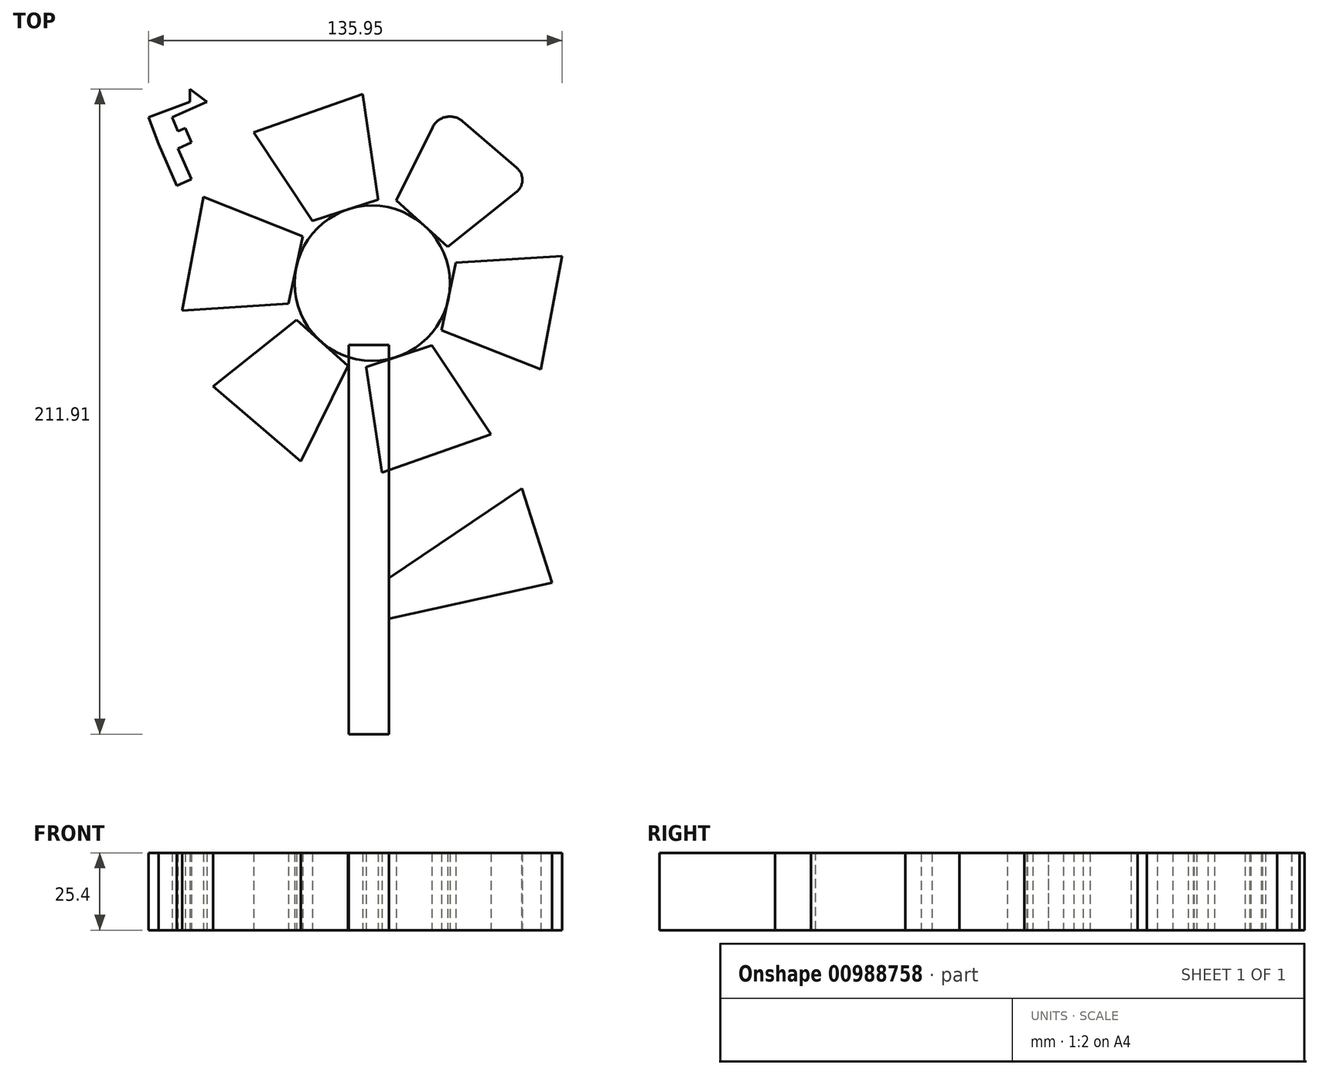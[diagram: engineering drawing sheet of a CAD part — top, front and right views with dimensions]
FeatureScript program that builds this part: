
annotation { "Feature Type Name" : "Feature", "Feature Type Description" : "" }
export const myFeature = defineFeature(function(context is Context, id is Id, definition is map)
    precondition{}
    {
        {
            var Q0;
            Q0=qCreatedBy(makeId("Top.planeOp"),FACE);
            var sketch = newSketch(context, id + "F0", { "sketchPlane" : qUnion([Q0])});
            skCircle(sketch, "E0", {"center": v(0, 0) * mm, "radius": 25.52 * mm});
            skLineSegment(sketch, "E1", {"start": v(7.91, 27.2) * mm, "end": v(24.8, 12.03) * mm});
            skLineSegment(sketch, "E2", {"start": v(24.8, 12.03) * mm, "end": v(52.24, 33.82) * mm});
            skLineSegment(sketch, "E3", {"start": v(52.24, 33.82) * mm, "end": v(29.66, 53.24) * mm});
            skLineSegment(sketch, "E4", {"start": v(19.83, 51.24) * mm, "end": v(7.91, 27.2) * mm});
            skLineSegment(sketch, "E5.1.0", {"start": v(-39, 49.6) * mm, "end": v(-19.6, 20.45) * mm});
            skLineSegment(sketch, "E5.1.1", {"start": v(-3.17, 62.15) * mm, "end": v(-39, 49.6) * mm});
            skLineSegment(sketch, "E5.1.2", {"start": v(1.98, 27.49) * mm, "end": v(-3.17, 62.15) * mm});
            skLineSegment(sketch, "E5.1.3", {"start": v(-19.6, 20.45) * mm, "end": v(1.98, 27.49) * mm});
            skLineSegment(sketch, "E5.2.0", {"start": v(-62.45, -8.97) * mm, "end": v(-27.51, -6.74) * mm});
            skLineSegment(sketch, "E5.2.1", {"start": v(-55.4, 28.33) * mm, "end": v(-62.45, -8.97) * mm});
            skLineSegment(sketch, "E5.2.2", {"start": v(-22.81, 15.46) * mm, "end": v(-55.4, 28.33) * mm});
            skLineSegment(sketch, "E5.2.3", {"start": v(-27.51, -6.74) * mm, "end": v(-22.81, 15.46) * mm});
            skLineSegment(sketch, "E5.3.0", {"start": v(-23.46, -58.57) * mm, "end": v(-7.91, -27.2) * mm});
            skLineSegment(sketch, "E5.3.1", {"start": v(-52.24, -33.82) * mm, "end": v(-23.46, -58.57) * mm});
            skLineSegment(sketch, "E5.3.2", {"start": v(-24.8, -12.03) * mm, "end": v(-52.24, -33.82) * mm});
            skLineSegment(sketch, "E5.3.3", {"start": v(-7.91, -27.2) * mm, "end": v(-24.8, -12.03) * mm});
            skLineSegment(sketch, "E5.4.0", {"start": v(39, -49.6) * mm, "end": v(19.6, -20.45) * mm});
            skLineSegment(sketch, "E5.4.1", {"start": v(3.17, -62.15) * mm, "end": v(39, -49.6) * mm});
            skLineSegment(sketch, "E5.4.2", {"start": v(-1.98, -27.49) * mm, "end": v(3.17, -62.15) * mm});
            skLineSegment(sketch, "E5.4.3", {"start": v(19.6, -20.45) * mm, "end": v(-1.98, -27.49) * mm});
            skLineSegment(sketch, "E5.5.0", {"start": v(62.45, 8.97) * mm, "end": v(27.51, 6.74) * mm});
            skLineSegment(sketch, "E5.5.1", {"start": v(55.4, -28.33) * mm, "end": v(62.45, 8.97) * mm});
            skLineSegment(sketch, "E5.5.2", {"start": v(22.81, -15.46) * mm, "end": v(55.4, -28.33) * mm});
            skLineSegment(sketch, "E5.5.3", {"start": v(27.51, 6.74) * mm, "end": v(22.81, -15.46) * mm});
            skPoint(sketch, "E6.visualSharp", {"position": v(23.46, 58.57) * mm});
            skArc(sketch, "E6.filletArc", {"start": v(29.66, 53.24) * mm, "mid": v(24.25, 54.64) * mm, "end": v(19.83, 51.24) * mm});
            skSolve(sketch);
        }
        {
            var Q0;
            {var subQ0=sQuery(id+"F0.wireOp",EDGE,"E0");var subQ4=makeQuery(id+"F0.imprint","INTERSECT",VERTEX,{"derivedFrom":[subQ0,sQuery(id+"F0.wireOp",EDGE,"E5.1.3")]});Q0=makeQuery(id+"F0.imprint","IMPRINT",FACE,{"disambiguationData":[TD([[makeQuery(id+"F0.imprint","IMPRINT",EDGE,{"disambiguationData":[TD([[subQ4,1.0]])],"derivedFrom":subQ0}),1.0]])]});}
            var Q1;
            {var subQ0=sQuery(id+"F0.wireOp",EDGE,"E2");Q1=makeQuery(id+"F0.imprint","IMPRINT",FACE,{"disambiguationData":[TD([[makeQuery(id+"F0.imprint","IMPRINT",EDGE,{"derivedFrom":subQ0}),1.0]])]});}
            var Q2;
            {var subQ1=sQuery(id+"F0.wireOp",EDGE,"E5.1.0");Q2=makeQuery(id+"F0.imprint","IMPRINT",FACE,{"disambiguationData":[TD([[makeQuery(id+"F0.imprint","IMPRINT",EDGE,{"derivedFrom":subQ1}),1.0]])]});}
            var Q3;
            {var subQ1=sQuery(id+"F0.wireOp",EDGE,"E5.2.0");Q3=makeQuery(id+"F0.imprint","IMPRINT",FACE,{"disambiguationData":[TD([[makeQuery(id+"F0.imprint","IMPRINT",EDGE,{"derivedFrom":subQ1}),1.0]])]});}
            var Q4;
            {var subQ1=sQuery(id+"F0.wireOp",EDGE,"E5.3.0");Q4=makeQuery(id+"F0.imprint","IMPRINT",FACE,{"disambiguationData":[TD([[makeQuery(id+"F0.imprint","IMPRINT",EDGE,{"derivedFrom":subQ1}),1.0]])]});}
            var Q5;
            {var subQ1=sQuery(id+"F0.wireOp",EDGE,"E5.4.0");Q5=makeQuery(id+"F0.imprint","IMPRINT",FACE,{"disambiguationData":[TD([[makeQuery(id+"F0.imprint","IMPRINT",EDGE,{"derivedFrom":subQ1}),1.0]])]});}
            var Q6;
            {var subQ1=sQuery(id+"F0.wireOp",EDGE,"E5.5.0");Q6=makeQuery(id+"F0.imprint","IMPRINT",FACE,{"disambiguationData":[TD([[makeQuery(id+"F0.imprint","IMPRINT",EDGE,{"derivedFrom":subQ1}),1.0]])]});}
            extrude(context, id + "F1", {"entities" : qUnion([Q0, Q1, Q2, Q3, Q4, Q5, Q6]), "depth" : 25.4 * mm, "offsetDistance" : 25.4 * mm});
        }
        {
            var Q0;
            Q0=makeQuery(id+"F1.opExtrude","CAP_FACE",FACE,{"disambiguationData":[OSD([sQuery(id+"F0.wireOp",EDGE,"E5.4.0"),sQuery(id+"F0.wireOp",EDGE,"E5.4.1"),sQuery(id+"F0.wireOp",EDGE,"E5.4.2"),sQuery(id+"F0.wireOp",EDGE,"E5.4.3")])],"isStart":false});
            var sketch = newSketch(context, id + "F2", { "sketchPlane" : qUnion([Q0])});
            skLineSegment(sketch, "E7.bottom", {"start": v(-7.73, -20.32) * mm, "end": v(5.51, -20.32) * mm});
            skLineSegment(sketch, "E7.top", {"start": v(-7.73, -148.1) * mm, "end": v(5.51, -148.1) * mm});
            skLineSegment(sketch, "E7.left", {"start": v(-7.73, -20.32) * mm, "end": v(-7.73, -148.1) * mm});
            skLineSegment(sketch, "E7.right", {"start": v(5.51, -20.32) * mm, "end": v(5.51, -148.1) * mm});
            skSolve(sketch);
        }
        {
            var Q0;
            Q0 = qSketchRegion(id + "F2", true);
            extrude(context, id + "F3", {"entities" : qUnion([Q0]), "oppositeDirection" : true, "depth" : 25.4 * mm, "offsetDistance" : 25.4 * mm});
        }
        {
            var Q0;
            Q0=makeQuery(id+"F3.opExtrude","CAP_FACE",FACE,{"disambiguationData":[OSD([sQuery(id+"F2.wireOp",EDGE,"E7.bottom"),sQuery(id+"F2.wireOp",EDGE,"E7.top"),sQuery(id+"F2.wireOp",EDGE,"E7.left"),sQuery(id+"F2.wireOp",EDGE,"E7.right")])],"isStart":true});
            var sketch = newSketch(context, id + "F4", { "sketchPlane" : qUnion([Q0])});
            skLineSegment(sketch, "E8", {"start": v(5.51, -96.88) * mm, "end": v(49.23, -67.4) * mm});
            skLineSegment(sketch, "E9", {"start": v(49.23, -67.4) * mm, "end": v(59.05, -98.39) * mm});
            skLineSegment(sketch, "E10", {"start": v(59.05, -98.39) * mm, "end": v(5.51, -110.22) * mm});
            skLineSegment(sketch, "E11", {"start": v(5.51, -110.22) * mm, "end": v(5.51, -96.88) * mm});
            skSolve(sketch);
        }
        {
            var Q0;
            Q0 = qSketchRegion(id + "F4", true);
            extrude(context, id + "F5", {"entities" : qUnion([Q0]), "oppositeDirection" : true, "depth" : 25.4 * mm, "offsetDistance" : 25.4 * mm});
        }
        {
            var Q0;
            Q0=makeQuery(id+"F1.opExtrude","SWEPT_EDGE",EDGE,{"disambiguationData":[OSD([sQuery(id+"F0.wireOp",EDGE,"E2"),sQuery(id+"F0.wireOp",EDGE,"E3")])]});
            fillet(context, id + "F6", {"entities" : qUnion([Q0]), "radius" : 5.08 * mm, "tangentPropagation" : true, "allowEdgeOverflow" : false});
        }
        {
            var Q0;
            Q0=qCreatedBy(makeId("Top.planeOp"),FACE);
            var sketch = newSketch(context, id + "F7", { "sketchPlane" : qUnion([Q0])});
            skLineSegment(sketch, "E12", {"start": v(-59.94, 59.57) * mm, "end": v(-73.5, 54.49) * mm});
            skLineSegment(sketch, "E13", {"start": v(-73.5, 54.49) * mm, "end": v(-70.2, 45.71) * mm});
            skLineSegment(sketch, "E14", {"start": v(-70.2, 45.71) * mm, "end": v(-64.18, 32.03) * mm});
            skLineSegment(sketch, "E15", {"start": v(-64.18, 32.03) * mm, "end": v(-59.34, 34.17) * mm});
            skLineSegment(sketch, "E16", {"start": v(-59.34, 34.17) * mm, "end": v(-63.78, 44.26) * mm});
            skLineSegment(sketch, "E17", {"start": v(-63.78, 44.26) * mm, "end": v(-59.34, 46.22) * mm});
            skLineSegment(sketch, "E18", {"start": v(-59.34, 46.22) * mm, "end": v(-61.42, 50.95) * mm});
            skLineSegment(sketch, "E19", {"start": v(-61.42, 50.95) * mm, "end": v(-63.78, 49.91) * mm});
            skLineSegment(sketch, "E20", {"start": v(-63.78, 49.91) * mm, "end": v(-65.8, 54.49) * mm});
            skLineSegment(sketch, "E21", {"start": v(-65.8, 54.49) * mm, "end": v(-54.32, 59.54) * mm});
            skLineSegment(sketch, "E22", {"start": v(-54.32, 59.54) * mm, "end": v(-59.94, 63.8) * mm});
            skLineSegment(sketch, "E23", {"start": v(-59.94, 63.8) * mm, "end": v(-59.94, 59.57) * mm});
            skSolve(sketch);
        }
        {
            var Q0;
            Q0 = qSketchRegion(id + "F7", true);
            extrude(context, id + "F8", {"entities" : qUnion([Q0]), "depth" : 25.4 * mm, "offsetDistance" : 25.4 * mm});
        }
    });
